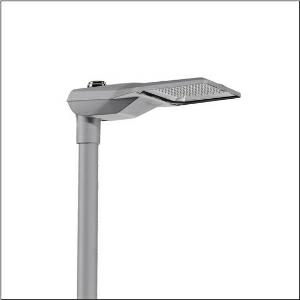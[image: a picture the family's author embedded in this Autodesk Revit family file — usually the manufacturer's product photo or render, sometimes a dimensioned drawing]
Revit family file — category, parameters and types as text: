
# Revit family: streetlight_sl_21_midi___st0_5a_5xe7b37n08nb_a99d
name_source: partatom
category: Lighting Fixtures
units: mm (PartAtom-declared; Revit-internal decimal feet)

## family parameters
Cut with Voids When Loaded = No
Host = Face
Light Source = No
Part Type = Normal
Room Calculation Point = No
Round Connector Dimension = Use Diameter
Shared = No

## types (1)
- --- (1 x LED, 22700 lm, 151.2 W, 3000K)
    Apparent Load = 151 VA
    CIE Flux Codes = 43 76 97 100 100
    Color Rendering = 70
    Color Temperature = 3000K
    Default Elevation = 1800 mm
    Description = Streetlight SL 21 midi, mast luminaire, primary light control with lens, of PMMA, primary optical cover: cover, of toughened safety glass, transparent, light distribution: ST0.5a, light emission: direct distribution, primary light characteristic: asymmetric, installation type: side-entry, LED, 3G 2.5mm², High Power LED, rated luminous flux: 22.700lm, luminous efficacy: 150lm/W, light colour: 730, colour temperature: 3000K, control gear: NEMA (7pin), control: overheat protection, pre-setting: linear dimming characteristic, constant luminous flux control, time-dependent luminous flux control, flexible luminous flux parameterisation, mains connection: 220..240V, AC, 50/60Hz, connection cable pre-assembled, cable length: 12,5m, wiring characteristics: H05VV-F, start of lifetime: 151W, end of service life: 157W, reduction: 70W, luminaire housing, of diecast aluminium (EN AC-44300), powder-coated, Siteco® metallic grey (DB 702S), corrosivity category C5 mid according to DIN EN ISO 12944, multi-level sealing system, sealing non-destructively replaceable, inclination adjustable: 0°, 5°, 10°, 15°, length: 644mm, width: 335mm, height: 110mm, spigot size: 42mm (side-entry), mounting height: 4..8m, protection rating (complete): IP66, insulation class (complete): insulation class I (protective earthing), certification: CE, ENEC, ENEC+, VDE, impact resistance: IK10, permissible operating ambient temperature for outdoor applications: -40..+50°C, standard-compliant lighting for roads and squares, packaging unit: 1 piece

Light Distribution: ST0.5a
    Height = 111 mm
    Lamp = 1 x LED
    Lamp Light Flux = 22700 lm
    Lamp Power = 151.2 W
    Lamp count = 1
    Length = 644 mm
    Luminous efficacy = 150 lm/W
    Manufacturer = Siteco
    ModVariant = No
    Model = 5XE7B37N08NB
    Number of Poles = 1
    OnlyDefault = Yes
    Power Factor = 1
    Product Name = Streetlight SL 21 midi | ST0.5a
    Product group = mast luminaire | pylon top
    ProductGroupID = 6100
    Protection Class = Protection class I
    Protection Degree = IP 66
    RLX_Detail_Level = 1
    RLX_Emergency_Light_Flux = 0 lm
    RLX_Emergency_Type = 0
    RLX_Emergency_Type_DB = No
    RlxData = <blob elided: 37761 chars, md5=ee4de532>
    Socket = socket
    Standby Power = 0 W
    System Light Flux = 22700 lm
    System Power = 151 W
    Type Comments = factory setting: luminous flux: 100 % | dim-lin: 254 | 802 mA
    Type Image = l_1294377.jpg
    URL = http://relux.com
    VarID = @adj_158171
    Voltage = 0 V
    Weight = 0.00 kg
    Width = 336 mm

## geometry (parser evidence)
native form markers: Blend x4, Sweep x10
no freeform markers — native parametric forms only
